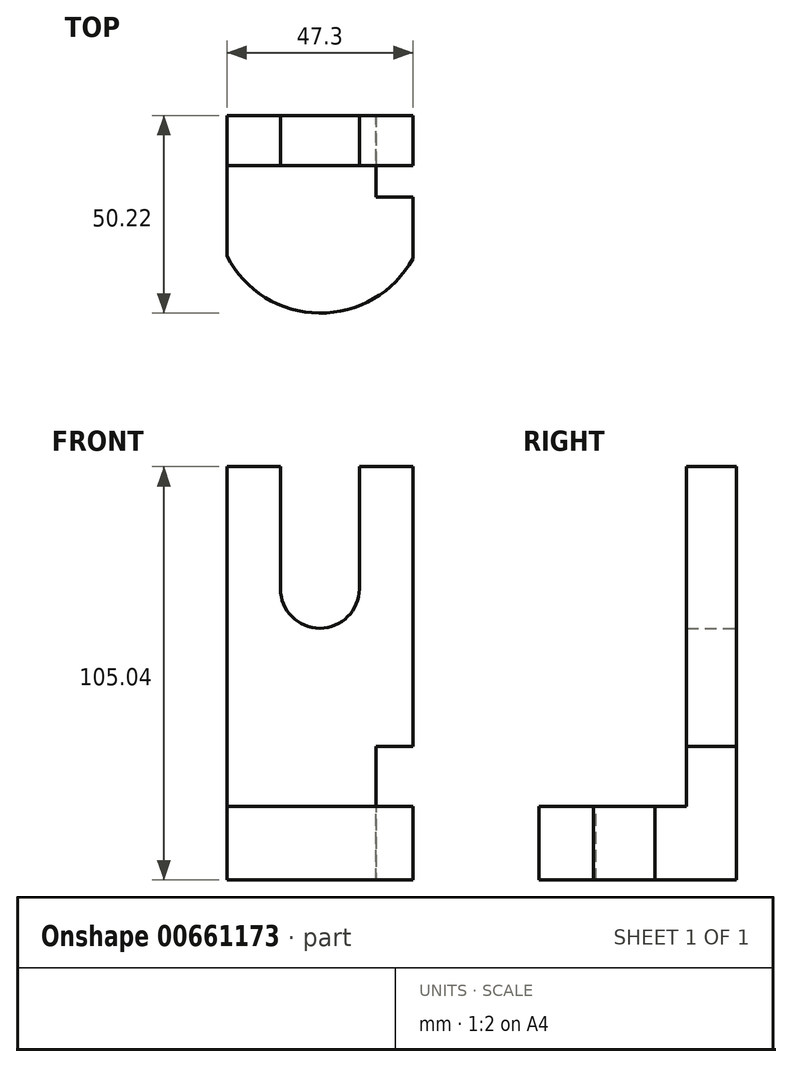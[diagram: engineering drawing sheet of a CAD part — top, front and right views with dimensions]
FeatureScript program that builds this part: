
annotation { "Feature Type Name" : "Feature", "Feature Type Description" : "" }
export const myFeature = defineFeature(function(context is Context, id is Id, definition is map)
    precondition{}
    {
        {
            var Q0;
            Q0=qCreatedBy(makeId("Front.planeOp"),FACE);
            var sketch = newSketch(context, id + "F0", { "sketchPlane" : qUnion([Q0])});
            skLineSegment(sketch, "E0.bottom", {"start": v(-23.65, 52.52) * mm, "end": v(-10.01, 52.52) * mm});
            skLineSegment(sketch, "E0.top", {"start": v(-23.65, -52.52) * mm, "end": v(23.65, -52.52) * mm});
            skLineSegment(sketch, "E0.left", {"start": v(-23.65, 52.52) * mm, "end": v(-23.65, -52.52) * mm});
            skLineSegment(sketch, "E0.right", {"start": v(23.65, 52.52) * mm, "end": v(23.65, -52.52) * mm});
            skPoint(sketch, "E0.middle", {"position": v(0, 0) * mm});
            skLineSegment(sketch, "E1.left", {"start": v(-10.01, 52.52) * mm, "end": v(-10.01, 21.47) * mm});
            skLineSegment(sketch, "E1.right", {"start": v(10.01, 52.52) * mm, "end": v(10.01, 21.47) * mm});
            skArc(sketch, "E2", {"start": v(-10.01, 21.47) * mm, "mid": v(0, 11.46) * mm, "end": v(10.01, 21.47) * mm});
            skLineSegment(sketch, "E3.trimOffspring", {"start": v(10.01, 52.52) * mm, "end": v(23.65, 52.52) * mm});
            skSolve(sketch);
        }
        {
            var Q0;
            Q0=qSketchRegion(id+"F0",true);
            extrude(context, id + "F1", {"entities" : qUnion([Q0]), "depth" : 12.7 * mm, "offsetDistance" : 25.4 * mm});
        }
        {
            var Q0;
            Q0=makeQuery(id+"F1.opExtrude","CAP_FACE",FACE,{"disambiguationData":[OSD([sQuery(id+"F0.wireOp",EDGE,"E0.bottom"),sQuery(id+"F0.wireOp",EDGE,"E0.top"),sQuery(id+"F0.wireOp",EDGE,"E0.left"),sQuery(id+"F0.wireOp",EDGE,"E0.right"),sQuery(id+"F0.wireOp",EDGE,"E1.left"),sQuery(id+"F0.wireOp",EDGE,"E1.right"),sQuery(id+"F0.wireOp",EDGE,"E2"),sQuery(id+"F0.wireOp",EDGE,"E3.trimOffspring")])],"isStart":false});
            var sketch = newSketch(context, id + "F2", { "sketchPlane" : qUnion([Q0])});
            skLineSegment(sketch, "E4.bottom", {"start": v(-23.65, -52.52) * mm, "end": v(23.65, -52.52) * mm});
            skLineSegment(sketch, "E4.top", {"start": v(-23.65, -33.82) * mm, "end": v(23.65, -33.82) * mm});
            skLineSegment(sketch, "E4.left", {"start": v(-23.65, -52.52) * mm, "end": v(-23.65, -33.82) * mm});
            skLineSegment(sketch, "E4.right", {"start": v(23.65, -52.52) * mm, "end": v(23.65, -33.82) * mm});
            skSolve(sketch);
        }
        {
            var Q0;
            Q0=qSketchRegion(id+"F2",true);
            extrude(context, id + "F3", {"entities" : qUnion([Q0]), "operationType" : NewBodyOperationType.ADD, "depth" : 38.35 * mm, "offsetDistance" : 25.4 * mm});
        }
        {
            var Q0;
            Q0=makeQuery(id+"F3.opExtrude","SWEPT_FACE",FACE,{"disambiguationData":[OSD([sQuery(id+"F2.wireOp",EDGE,"E4.top")])]});
            var sketch = newSketch(context, id + "F4", { "sketchPlane" : qUnion([Q0])});
            skArc(sketch, "E5", {"start": v(-23.65, -35.77) * mm, "mid": v(-0.18, -50.21) * mm, "end": v(23.65, -36.37) * mm});
            skSolve(sketch);
        }
        {
            var Q0;
            {var subQ0=sQuery(id+"F4.wireOp",EDGE,"E5");Q0=makeQuery(id+"F4.imprint","IMPRINT",FACE,{"disambiguationData":[TD([[makeQuery(id+"F4.imprint","IMPRINT",EDGE,{"derivedFrom":subQ0}),-1.0]])]});}
            extrude(context, id + "F5", {"entities" : qUnion([Q0]), "operationType" : NewBodyOperationType.REMOVE, "oppositeDirection" : true, "depth" : 25.4 * mm, "offsetDistance" : 25.4 * mm});
        }
        {
            var Q0;
            Q0=makeQuery(id+"F3.boolean.opBoolean","MERGE",FACE,{"derivedFrom":[makeQuery(id+"F1.opExtrude","SWEPT_FACE",FACE,{"disambiguationData":[OSD([sQuery(id+"F0.wireOp",EDGE,"E0.right")])]}),makeQuery(id+"F3.opExtrude","SWEPT_FACE",FACE,{"disambiguationData":[OSD([sQuery(id+"F2.wireOp",EDGE,"E4.right")])]})]});
            var sketch = newSketch(context, id + "F6", { "sketchPlane" : qUnion([Q0])});
            skLineSegment(sketch, "E6.bottom", {"start": v(0, -52.52) * mm, "end": v(-20.73, -52.52) * mm});
            skLineSegment(sketch, "E6.top", {"start": v(0, -18.56) * mm, "end": v(-20.73, -18.56) * mm});
            skLineSegment(sketch, "E6.left", {"start": v(0, -52.52) * mm, "end": v(0, -18.56) * mm});
            skLineSegment(sketch, "E6.right", {"start": v(-20.73, -52.52) * mm, "end": v(-20.73, -18.56) * mm});
            skSolve(sketch);
        }
        {
            var Q0;
            Q0=qSketchRegion(id+"F6",true);
            extrude(context, id + "F7", {"entities" : qUnion([Q0]), "operationType" : NewBodyOperationType.REMOVE, "oppositeDirection" : true, "depth" : 9.4 * mm, "offsetDistance" : 25.4 * mm});
        }
    });
